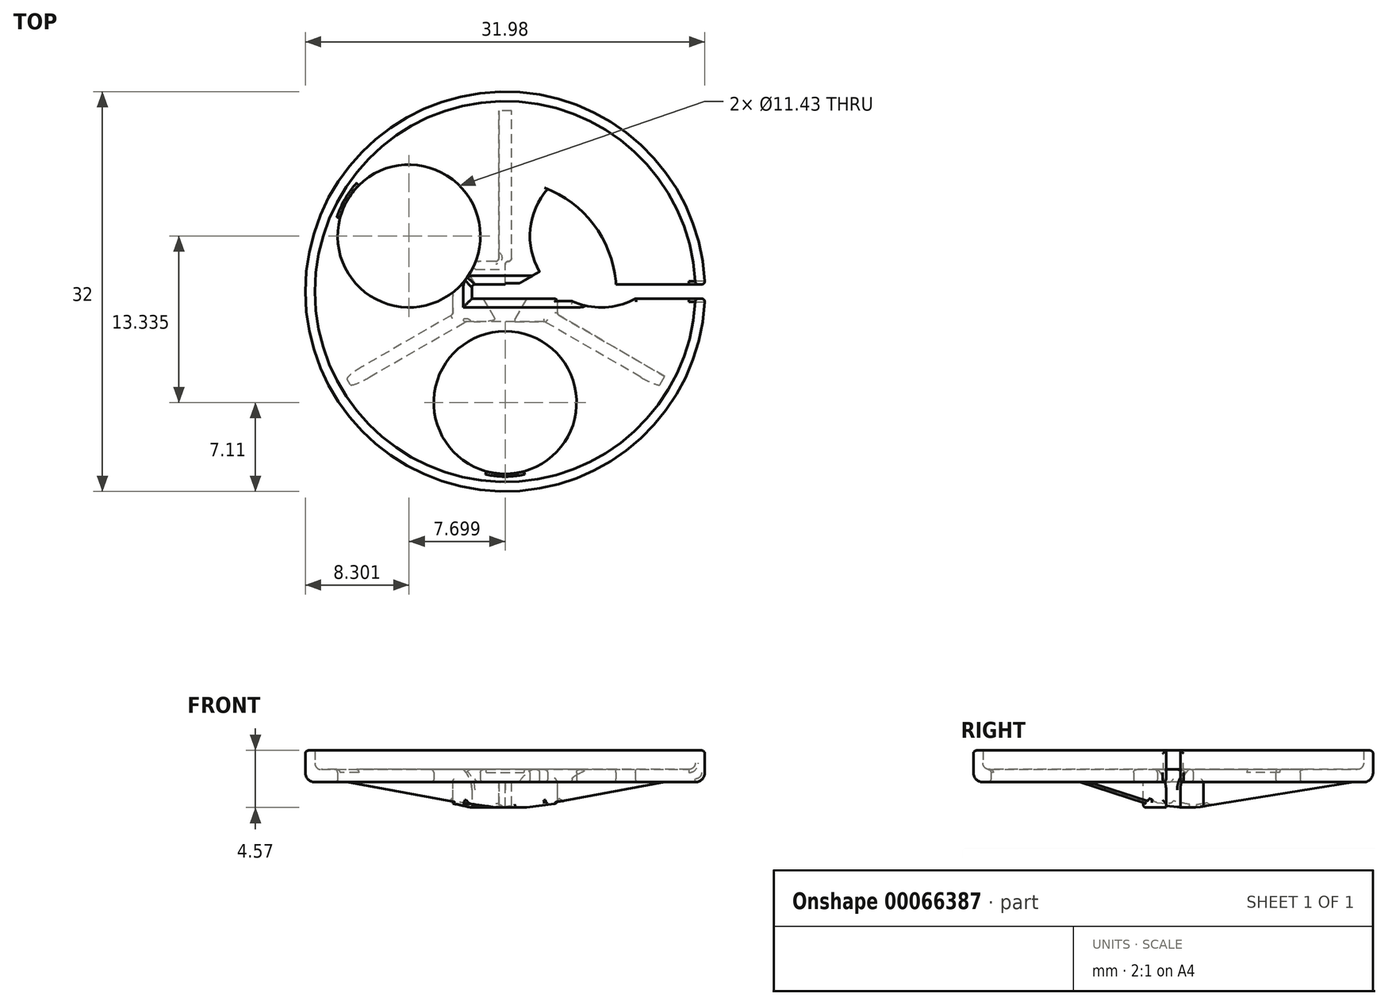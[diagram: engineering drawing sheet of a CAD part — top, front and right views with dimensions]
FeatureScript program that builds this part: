
annotation { "Feature Type Name" : "Feature", "Feature Type Description" : "" }
export const myFeature = defineFeature(function(context is Context, id is Id, definition is map)
    precondition{}
    {
        {
            var Q0;
            Q0=qCreatedBy(makeId("Top.planeOp"),FACE);
            var sketch = newSketch(context, id + "F0", { "sketchPlane" : qUnion([Q0])});
            skCircle(sketch, "E0", {"center": v(0, 0) * mm, "radius": 15.24 * mm});
            skCircle(sketch, "E1", {"center": v(0, 0) * mm, "radius": 16 * mm});
            skLineSegment(sketch, "E2.rect.bottom", {"start": v(20.24, 0.57) * mm, "end": v(-2.67, 0.57) * mm});
            skLineSegment(sketch, "E2.rect.top", {"start": v(20.24, -0.57) * mm, "end": v(-2.67, -0.57) * mm});
            skLineSegment(sketch, "E2.rect.left", {"start": v(20.24, 0.57) * mm, "end": v(20.24, -0.57) * mm});
            skLineSegment(sketch, "E2.rect.right", {"start": v(-2.67, 0.57) * mm, "end": v(-2.67, -0.57) * mm});
            skPoint(sketch, "E2.rect.middle", {"position": v(8.79, 0) * mm});
            skLineSegment(sketch, "E3.rect.bottom", {"start": v(1.65, 13.2) * mm, "end": v(-1.65, 13.2) * mm});
            skLineSegment(sketch, "E3.rect.top", {"start": v(1.65, 11.68) * mm, "end": v(-1.65, 11.68) * mm});
            skLineSegment(sketch, "E3.rect.left", {"start": v(1.65, 13.2) * mm, "end": v(1.65, 11.68) * mm});
            skLineSegment(sketch, "E3.rect.right", {"start": v(-1.65, 13.2) * mm, "end": v(-1.65, 11.68) * mm});
            skPoint(sketch, "E3.rect.middle", {"position": v(0, 12.45) * mm});
            skLineSegment(sketch, "E4", {"start": v(0, 0) * mm, "end": v(-13.86, -8) * mm});
            skLineSegment(sketch, "E5", {"start": v(0, 0) * mm, "end": v(13.86, -8) * mm});
            skLineSegment(sketch, "E6", {"start": v(-12.26, -5.17) * mm, "end": v(-10.61, -8.03) * mm});
            skLineSegment(sketch, "E7", {"start": v(-10.61, -8.03) * mm, "end": v(-9.3, -7.27) * mm});
            skLineSegment(sketch, "E8", {"start": v(-9.3, -7.27) * mm, "end": v(-10.94, -4.41) * mm});
            skLineSegment(sketch, "E9", {"start": v(-10.94, -4.41) * mm, "end": v(-12.26, -5.17) * mm});
            skLineSegment(sketch, "E10", {"start": v(12.26, -5.17) * mm, "end": v(10.61, -8.03) * mm});
            skLineSegment(sketch, "E11", {"start": v(10.61, -8.03) * mm, "end": v(9.3, -7.27) * mm});
            skLineSegment(sketch, "E12", {"start": v(9.3, -7.27) * mm, "end": v(10.94, -4.41) * mm});
            skLineSegment(sketch, "E13", {"start": v(10.94, -4.41) * mm, "end": v(12.26, -5.17) * mm});
            skCircle(sketch, "E14", {"center": v(0, 0) * mm, "radius": 8.9 * mm});
            skLineSegment(sketch, "E15", {"start": v(0, 0) * mm, "end": v(-7.7, 4.44) * mm});
            skLineSegment(sketch, "E16", {"start": v(0, 0) * mm, "end": v(7.7, 4.44) * mm});
            skLineSegment(sketch, "E17", {"start": v(0, 0) * mm, "end": v(0, -8.9) * mm});
            skCircle(sketch, "E18", {"center": v(-7.7, 4.44) * mm, "radius": 5.72 * mm});
            skCircle(sketch, "E19", {"center": v(7.7, 4.44) * mm, "radius": 5.72 * mm});
            skCircle(sketch, "E20", {"center": v(0, -8.9) * mm, "radius": 5.72 * mm});
            skSolve(sketch);
        }
        {
            var Q0;
            {var subQ0=sQuery(id+"F0.wireOp",EDGE,"E2.rect.bottom");var subQ1=sQuery(id+"F0.wireOp",EDGE,"E0");var subQ2=makeQuery(id+"F0.imprint","INTERSECT",VERTEX,{"derivedFrom":[subQ1,subQ0]});Q0=makeQuery(id+"F0.imprint","IMPRINT",FACE,{"disambiguationData":[TD([[makeQuery(id+"F0.imprint","IMPRINT",EDGE,{"disambiguationData":[TD([[subQ2,-1.0]])],"derivedFrom":subQ1}),-1.0]])]});}
            var Q1;
            {var subQ5=sQuery(id+"F0.wireOp",EDGE,"E2.rect.right");Q1=makeQuery(id+"F0.imprint","IMPRINT",FACE,{"disambiguationData":[TD([[makeQuery(id+"F0.imprint","IMPRINT",EDGE,{"derivedFrom":subQ5}),-1.0]])]});}
            var Q2;
            {var subQ1=sQuery(id+"F0.wireOp",EDGE,"E7");Q2=makeQuery(id+"F0.imprint","IMPRINT",FACE,{"disambiguationData":[TD([[makeQuery(id+"F0.imprint","IMPRINT",EDGE,{"derivedFrom":subQ1}),-1.0]])]});}
            var Q3;
            {var subQ5=sQuery(id+"F0.wireOp",EDGE,"E7");Q3=makeQuery(id+"F0.imprint","IMPRINT",FACE,{"disambiguationData":[TD([[makeQuery(id+"F0.imprint","IMPRINT",EDGE,{"derivedFrom":subQ5}),1.0]])]});}
            var Q4;
            {var subQ5=sQuery(id+"F0.wireOp",EDGE,"E9");Q4=makeQuery(id+"F0.imprint","IMPRINT",FACE,{"disambiguationData":[TD([[makeQuery(id+"F0.imprint","IMPRINT",EDGE,{"derivedFrom":subQ5}),1.0]])]});}
            var Q5;
            Q5=makeQuery(id+"F0.imprint","IMPRINT",FACE,{"disambiguationData":[TD([[makeQuery(id+"F0.imprint","IMPRINT",EDGE,{"derivedFrom":sQuery(id+"F0.wireOp",EDGE,"E3.rect.bottom")}),1.0]])]});
            var Q6;
            {var subQ5=sQuery(id+"F0.wireOp",EDGE,"E13");Q6=makeQuery(id+"F0.imprint","IMPRINT",FACE,{"disambiguationData":[TD([[makeQuery(id+"F0.imprint","IMPRINT",EDGE,{"derivedFrom":subQ5}),-1.0]])]});}
            var Q7;
            {var subQ5=sQuery(id+"F0.wireOp",EDGE,"E11");Q7=makeQuery(id+"F0.imprint","IMPRINT",FACE,{"disambiguationData":[TD([[makeQuery(id+"F0.imprint","IMPRINT",EDGE,{"derivedFrom":subQ5}),-1.0]])]});}
            var Q8;
            {var subQ10=sQuery(id+"F0.wireOp",EDGE,"E13");Q8=makeQuery(id+"F0.imprint","IMPRINT",FACE,{"disambiguationData":[TD([[makeQuery(id+"F0.imprint","IMPRINT",EDGE,{"derivedFrom":subQ10}),1.0]])]});}
            var Q9;
            {var subQ0=sQuery(id+"F0.wireOp",EDGE,"E4");var subQ1=sQuery(id+"F0.wireOp",EDGE,"E0");var subQ2=makeQuery(id+"F0.imprint","INTERSECT",VERTEX,{"derivedFrom":[subQ1,subQ0]});Q9=makeQuery(id+"F0.imprint","IMPRINT",FACE,{"disambiguationData":[TD([[makeQuery(id+"F0.imprint","IMPRINT",EDGE,{"disambiguationData":[TD([[subQ2,-1.0]])],"derivedFrom":subQ1}),-1.0]])]});}
            var Q10;
            {var subQ0=sQuery(id+"F0.wireOp",EDGE,"E5");var subQ1=sQuery(id+"F0.wireOp",EDGE,"E0");var subQ2=makeQuery(id+"F0.imprint","INTERSECT",VERTEX,{"derivedFrom":[subQ1,subQ0]});Q10=makeQuery(id+"F0.imprint","IMPRINT",FACE,{"disambiguationData":[TD([[makeQuery(id+"F0.imprint","IMPRINT",EDGE,{"disambiguationData":[TD([[subQ2,-1.0]])],"derivedFrom":subQ1}),-1.0]])]});}
            var Q11;
            Q11=makeQuery(id+"F0.imprint","IMPRINT",FACE,{"disambiguationData":[TD([[makeQuery(id+"F0.imprint","IMPRINT",EDGE,{"derivedFrom":sQuery(id+"F0.wireOp",EDGE,"E3.rect.bottom")}),-1.0]])]});
            var Q12;
            {var subQ1=sQuery(id+"F0.wireOp",EDGE,"E2.rect.bottom");var subQ5=sQuery(id+"F0.wireOp",EDGE,"E16");var subQ6=makeQuery(id+"F0.imprint","INTERSECT",VERTEX,{"derivedFrom":[subQ1,subQ5]});Q12=makeQuery(id+"F0.imprint","IMPRINT",FACE,{"disambiguationData":[TD([[makeQuery(id+"F0.imprint","IMPRINT",EDGE,{"disambiguationData":[TD([[subQ6,-1.0]])],"derivedFrom":subQ1}),-1.0]])]});}
            var Q13;
            {var subQ1=sQuery(id+"F0.wireOp",EDGE,"E2.rect.top");var subQ5=sQuery(id+"F0.wireOp",EDGE,"E5");var subQ6=makeQuery(id+"F0.imprint","INTERSECT",VERTEX,{"derivedFrom":[subQ1,subQ5]});Q13=makeQuery(id+"F0.imprint","IMPRINT",FACE,{"disambiguationData":[TD([[makeQuery(id+"F0.imprint","IMPRINT",EDGE,{"disambiguationData":[TD([[subQ6,-1.0]])],"derivedFrom":subQ1}),1.0]])]});}
            var Q14;
            {var subQ0=sQuery(id+"F0.wireOp",EDGE,"E17");var subQ1=sQuery(id+"F0.wireOp",EDGE,"E2.rect.top");var subQ2=makeQuery(id+"F0.imprint","INTERSECT",VERTEX,{"derivedFrom":[subQ1,subQ0]});Q14=makeQuery(id+"F0.imprint","IMPRINT",FACE,{"disambiguationData":[TD([[makeQuery(id+"F0.imprint","IMPRINT",EDGE,{"disambiguationData":[TD([[subQ2,-1.0]])],"derivedFrom":subQ1}),1.0]])]});}
            var Q15;
            {var subQ0=sQuery(id+"F0.wireOp",EDGE,"E19");var subQ1=sQuery(id+"F0.wireOp",EDGE,"E2.rect.top");var subQ2=makeQuery(id+"F0.imprint","INTERSECT",VERTEX,{"disambiguationData":[OD(1.0)],"derivedFrom":[subQ1,subQ0]});Q15=makeQuery(id+"F0.imprint","IMPRINT",FACE,{"disambiguationData":[TD([[makeQuery(id+"F0.imprint","IMPRINT",EDGE,{"disambiguationData":[TD([[subQ2,-1.0]])],"derivedFrom":subQ1}),1.0]])]});}
            var Q16;
            {var subQ0=sQuery(id+"F0.wireOp",EDGE,"E19");var subQ1=sQuery(id+"F0.wireOp",EDGE,"E2.rect.bottom");var subQ2=makeQuery(id+"F0.imprint","INTERSECT",VERTEX,{"disambiguationData":[OD(1.0)],"derivedFrom":[subQ1,subQ0]});Q16=makeQuery(id+"F0.imprint","IMPRINT",FACE,{"disambiguationData":[TD([[makeQuery(id+"F0.imprint","IMPRINT",EDGE,{"disambiguationData":[TD([[subQ2,-1.0]])],"derivedFrom":subQ1}),-1.0]])]});}
            extrude(context, id + "F1", {"entities" : qUnion([Q0, Q1, Q2, Q3, Q4, Q5, Q6, Q7, Q8, Q9, Q10, Q11, Q12, Q13, Q14, Q15, Q16]), "depth" : 1.02 * mm});
        }
        {
            var Q0;
            {var subQ0=sQuery(id+"F0.wireOp",EDGE,"E2.rect.bottom");var subQ1=sQuery(id+"F0.wireOp",EDGE,"E0");var subQ2=makeQuery(id+"F0.imprint","INTERSECT",VERTEX,{"derivedFrom":[subQ1,subQ0]});Q0=makeQuery(id+"F0.imprint","IMPRINT",FACE,{"disambiguationData":[TD([[makeQuery(id+"F0.imprint","IMPRINT",EDGE,{"disambiguationData":[TD([[subQ2,-1.0]])],"derivedFrom":subQ1}),-1.0]])]});}
            var Q1;
            {var subQ0=sQuery(id+"F0.wireOp",EDGE,"E4");var subQ1=sQuery(id+"F0.wireOp",EDGE,"E0");var subQ2=makeQuery(id+"F0.imprint","INTERSECT",VERTEX,{"derivedFrom":[subQ1,subQ0]});Q1=makeQuery(id+"F0.imprint","IMPRINT",FACE,{"disambiguationData":[TD([[makeQuery(id+"F0.imprint","IMPRINT",EDGE,{"disambiguationData":[TD([[subQ2,-1.0]])],"derivedFrom":subQ1}),-1.0]])]});}
            var Q2;
            {var subQ0=sQuery(id+"F0.wireOp",EDGE,"E5");var subQ1=sQuery(id+"F0.wireOp",EDGE,"E0");var subQ2=makeQuery(id+"F0.imprint","INTERSECT",VERTEX,{"derivedFrom":[subQ1,subQ0]});Q2=makeQuery(id+"F0.imprint","IMPRINT",FACE,{"disambiguationData":[TD([[makeQuery(id+"F0.imprint","IMPRINT",EDGE,{"disambiguationData":[TD([[subQ2,-1.0]])],"derivedFrom":subQ1}),-1.0]])]});}
            extrude(context, id + "F2", {"entities" : qUnion([Q0, Q1, Q2]), "operationType" : NewBodyOperationType.ADD, "depth" : 2.54 * mm});
        }
        {
            var Q0;
            Q0=makeQuery(id+"F1.opExtrude","CAP_FACE",FACE,{"disambiguationData":[OSD([sQuery(id+"F0.wireOp",EDGE,"E1"),sQuery(id+"F0.wireOp",EDGE,"E2.rect.bottom"),sQuery(id+"F0.wireOp",EDGE,"E2.rect.top"),sQuery(id+"F0.wireOp",EDGE,"E2.rect.right"),sQuery(id+"F0.wireOp",EDGE,"E18"),sQuery(id+"F0.wireOp",EDGE,"E19"),sQuery(id+"F0.wireOp",EDGE,"E20")])],"isStart":true});
            var sketch = newSketch(context, id + "F3", { "sketchPlane" : qUnion([Q0])});
            skLineSegment(sketch, "E21.rect.bottom", {"start": v(4.2, 2.41) * mm, "end": v(-4.2, 2.41) * mm});
            skLineSegment(sketch, "E21.rect.top", {"start": v(4.2, -2.41) * mm, "end": v(-4.2, -2.41) * mm});
            skLineSegment(sketch, "E21.rect.left", {"start": v(4.2, 2.41) * mm, "end": v(4.2, -2.41) * mm});
            skLineSegment(sketch, "E21.rect.right", {"start": v(-4.2, 2.41) * mm, "end": v(-4.2, -2.41) * mm});
            skPoint(sketch, "E21.rect.middle", {"position": v(0, 0) * mm});
            skLineSegment(sketch, "E22", {"start": v(0, 0) * mm, "end": v(-13.86, 8) * mm});
            skLineSegment(sketch, "E23", {"start": v(0, 0) * mm, "end": v(13.86, 8) * mm});
            skLineSegment(sketch, "E24", {"start": v(0, 0) * mm, "end": v(0, -16) * mm});
            skLineSegment(sketch, "E25.bottom", {"start": v(-0.5, -2.41) * mm, "end": v(0.5, -2.41) * mm});
            skLineSegment(sketch, "E25.top", {"start": v(-0.5, -14.48) * mm, "end": v(0.5, -14.48) * mm});
            skLineSegment(sketch, "E25.left", {"start": v(-0.5, -2.41) * mm, "end": v(-0.5, -14.48) * mm});
            skLineSegment(sketch, "E25.right", {"start": v(0.5, -2.41) * mm, "end": v(0.5, -14.48) * mm});
            skLineSegment(sketch, "E26", {"start": v(-4.2, 1.83) * mm, "end": v(-12.8, 6.8) * mm});
            skLineSegment(sketch, "E27", {"start": v(-12.8, 6.8) * mm, "end": v(-12.28, 7.68) * mm});
            skLineSegment(sketch, "E28", {"start": v(-12.28, 7.68) * mm, "end": v(-3.16, 2.41) * mm});
            skLineSegment(sketch, "E29", {"start": v(4.2, 1.83) * mm, "end": v(12.8, 6.8) * mm});
            skLineSegment(sketch, "E30", {"start": v(12.8, 6.8) * mm, "end": v(12.28, 7.68) * mm});
            skLineSegment(sketch, "E31", {"start": v(12.28, 7.68) * mm, "end": v(3.16, 2.41) * mm});
            skSolve(sketch);
        }
        {
            var Q0;
            {var subQ1=sQuery(id+"F3.wireOp",EDGE,"E21.rect.bottom");Q0=makeQuery(id+"F3.imprint","IMPRINT",FACE,{"disambiguationData":[TD([[makeQuery(id+"F3.imprint","IMPRINT",EDGE,{"derivedFrom":subQ1}),1.0]])]});}
            var Q1;
            {var subQ0=sQuery(id+"F3.wireOp",EDGE,"E28");Q1=makeQuery(id+"F3.imprint","IMPRINT",FACE,{"disambiguationData":[TD([[makeQuery(id+"F3.imprint","IMPRINT",EDGE,{"derivedFrom":subQ0}),-1.0]])]});}
            var Q2;
            {var subQ0=sQuery(id+"F3.wireOp",EDGE,"E26");Q2=makeQuery(id+"F3.imprint","IMPRINT",FACE,{"disambiguationData":[TD([[makeQuery(id+"F3.imprint","IMPRINT",EDGE,{"derivedFrom":subQ0}),-1.0]])]});}
            var Q3;
            {var subQ0=sQuery(id+"F0.wireOp",EDGE,"E2.rect.right");var subQ1=makeQuery(id+"F1.opExtrude","CAP_EDGE",EDGE,{"disambiguationData":[OSD([subQ0])],"isStart":true});Q3=makeQuery(id+"F3.imprint","IMPRINT",FACE,{"disambiguationData":[TD([[makeQuery(id+"F3.imprint","IMPRINT",EDGE,{"derivedFrom":subQ1}),1.0]])]});}
            var Q4;
            {var subQ11=sQuery(id+"F3.wireOp",EDGE,"E24");var subQ13=sQuery(id+"F3.wireOp",EDGE,"E25.bottom");var subQ16=makeQuery(id+"F3.imprint","INTERSECT",VERTEX,{"derivedFrom":[subQ11,subQ13]});Q4=makeQuery(id+"F3.imprint","IMPRINT",FACE,{"disambiguationData":[TD([[makeQuery(id+"F3.imprint","IMPRINT",EDGE,{"disambiguationData":[TD([[subQ16,-1.0]])],"derivedFrom":subQ13}),1.0]])]});}
            var Q5;
            {var subQ1=sQuery(id+"F3.wireOp",EDGE,"E21.rect.bottom");var subQ9=sQuery(id+"F3.wireOp",EDGE,"E21.rect.left");var subQ10=makeQuery(id+"F3.imprint","INTERSECT",VERTEX,{"derivedFrom":[subQ1,subQ9]});Q5=makeQuery(id+"F3.imprint","IMPRINT",FACE,{"disambiguationData":[TD([[makeQuery(id+"F3.imprint","IMPRINT",EDGE,{"disambiguationData":[TD([[subQ10,-1.0]])],"derivedFrom":subQ1}),1.0]])]});}
            var Q6;
            {var subQ0=sQuery(id+"F3.wireOp",EDGE,"E29");Q6=makeQuery(id+"F3.imprint","IMPRINT",FACE,{"disambiguationData":[TD([[makeQuery(id+"F3.imprint","IMPRINT",EDGE,{"derivedFrom":subQ0}),1.0]])]});}
            var Q7;
            {var subQ0=sQuery(id+"F3.wireOp",EDGE,"E31");Q7=makeQuery(id+"F3.imprint","IMPRINT",FACE,{"disambiguationData":[TD([[makeQuery(id+"F3.imprint","IMPRINT",EDGE,{"derivedFrom":subQ0}),1.0]])]});}
            var Q8;
            {var subQ5=sQuery(id+"F3.wireOp",EDGE,"E25.right");Q8=makeQuery(id+"F3.imprint","IMPRINT",FACE,{"disambiguationData":[TD([[makeQuery(id+"F3.imprint","IMPRINT",EDGE,{"derivedFrom":subQ5}),-1.0]])]});}
            var Q9;
            {var subQ5=sQuery(id+"F3.wireOp",EDGE,"E25.left");Q9=makeQuery(id+"F3.imprint","IMPRINT",FACE,{"disambiguationData":[TD([[makeQuery(id+"F3.imprint","IMPRINT",EDGE,{"derivedFrom":subQ5}),1.0]])]});}
            extrude(context, id + "F4", {"entities" : qUnion([Q0, Q1, Q2, Q3, Q4, Q5, Q6, Q7, Q8, Q9]), "operationType" : NewBodyOperationType.ADD, "depth" : 2.03 * mm});
        }
        {
            var Q0;
            {var subQ0=sQuery(id+"F0.wireOp",EDGE,"E2.rect.bottom");var subQ2=makeQuery(id+"F0.imprint","INTERSECT",VERTEX,{"derivedFrom":[subQ0,sQuery(id+"F0.wireOp",EDGE,"E16")]});Q0=makeQuery(id+"F1.opExtrude","CAP_EDGE",EDGE,{"disambiguationData":[OSD([subQ0]),TDD([makeQuery(id+"F0.imprint","IMPRINT",EDGE,{"disambiguationData":[TD([[makeQuery(id+"F0.imprint","INTERSECT",VERTEX,{"disambiguationData":[OD(1.0)],"derivedFrom":[subQ0,sQuery(id+"F0.wireOp",EDGE,"E19")]}),-1.0]])],"derivedFrom":subQ0}),makeQuery(id+"F0.imprint","IMPRINT",EDGE,{"disambiguationData":[TD([[subQ2,-1.0]])],"derivedFrom":subQ0}),makeQuery(id+"F0.imprint","IMPRINT",EDGE,{"disambiguationData":[TD([[makeQuery(id+"F0.imprint","INTERSECT",VERTEX,{"derivedFrom":[subQ0,sQuery(id+"F0.wireOp",EDGE,"E2.rect.right")]}),1.0]])],"derivedFrom":subQ0})])],"isStart":false});}
            var Q1;
            {var subQ0=sQuery(id+"F0.wireOp",EDGE,"E2.rect.top");var subQ2=makeQuery(id+"F0.imprint","INTERSECT",VERTEX,{"derivedFrom":[subQ0,sQuery(id+"F0.wireOp",EDGE,"E17")]});var subQ3=makeQuery(id+"F0.imprint","INTERSECT",VERTEX,{"derivedFrom":[subQ0,sQuery(id+"F0.wireOp",EDGE,"E5")]});Q1=makeQuery(id+"F1.opExtrude","CAP_EDGE",EDGE,{"disambiguationData":[OSD([subQ0]),TDD([makeQuery(id+"F0.imprint","IMPRINT",EDGE,{"disambiguationData":[TD([[makeQuery(id+"F0.imprint","INTERSECT",VERTEX,{"disambiguationData":[OD(1.0)],"derivedFrom":[subQ0,sQuery(id+"F0.wireOp",EDGE,"E19")]}),-1.0]])],"derivedFrom":subQ0}),makeQuery(id+"F0.imprint","IMPRINT",EDGE,{"disambiguationData":[TD([[subQ3,-1.0]])],"derivedFrom":subQ0}),makeQuery(id+"F0.imprint","IMPRINT",EDGE,{"disambiguationData":[TD([[subQ2,-1.0]])],"derivedFrom":subQ0}),makeQuery(id+"F0.imprint","IMPRINT",EDGE,{"disambiguationData":[TD([[makeQuery(id+"F0.imprint","INTERSECT",VERTEX,{"derivedFrom":[subQ0,sQuery(id+"F0.wireOp",EDGE,"E2.rect.right")]}),1.0]])],"derivedFrom":subQ0})])],"isStart":false});}
            var Q2;
            Q2=makeQuery(id+"F1.opExtrude","CAP_EDGE",EDGE,{"disambiguationData":[OSD([sQuery(id+"F0.wireOp",EDGE,"E2.rect.right")])],"isStart":false});
            chamfer(context, id + "F5", {"entities" : qUnion([Q0, Q1, Q2]), "width" : 0.69 * mm, "tangentPropagation" : true});
        }
        {
            var Q0;
            {var subQ0=sQuery(id+"F0.wireOp",EDGE,"E2.rect.bottom");var subQ2=makeQuery(id+"F0.imprint","IMPRINT",EDGE,{"disambiguationData":[TD([[makeQuery(id+"F0.imprint","INTERSECT",VERTEX,{"derivedFrom":[subQ0,sQuery(id+"F0.wireOp",EDGE,"E2.rect.right")]}),1.0]])],"derivedFrom":subQ0});var subQ3=makeQuery(id+"F0.imprint","INTERSECT",VERTEX,{"derivedFrom":[subQ0,sQuery(id+"F0.wireOp",EDGE,"E16")]});var subQ4=makeQuery(id+"F0.imprint","IMPRINT",EDGE,{"disambiguationData":[TD([[subQ3,-1.0]])],"derivedFrom":subQ0});var subQ5=makeQuery(id+"F0.imprint","IMPRINT",EDGE,{"disambiguationData":[TD([[makeQuery(id+"F0.imprint","INTERSECT",VERTEX,{"disambiguationData":[OD(1.0)],"derivedFrom":[subQ0,sQuery(id+"F0.wireOp",EDGE,"E19")]}),-1.0]])],"derivedFrom":subQ0});Q0=makeQuery(id+"F5.opChamfer","BLEND_EDGE",EDGE,{"blendedFrom":[makeQuery(id+"F1.opExtrude","CAP_EDGE",EDGE,{"disambiguationData":[OSD([subQ0]),TDD([subQ5,subQ4,subQ2])],"isStart":false}),makeQuery(id+"F4.boolean.opBoolean","MERGE",FACE,{"derivedFrom":[makeQuery(id+"F1.opExtrude","SWEPT_FACE",FACE,{"disambiguationData":[OSD([subQ0]),TDD([subQ5,subQ4,subQ2])]}),makeQuery(id+"F4.opExtrude","SWEPT_FACE",FACE,{"disambiguationData":[OSD([subQ0])]})]})],"blendedInto":[makeQuery(id+"F4.boolean.opBoolean","MERGE",FACE,{"derivedFrom":[makeQuery(id+"F1.opExtrude","SWEPT_FACE",FACE,{"disambiguationData":[OSD([subQ0]),TDD([subQ5,subQ4,subQ2])]}),makeQuery(id+"F4.opExtrude","SWEPT_FACE",FACE,{"disambiguationData":[OSD([subQ0])]})]})]});}
            var Q1;
            {var subQ0=sQuery(id+"F0.wireOp",EDGE,"E2.rect.right");Q1=makeQuery(id+"F5.opChamfer","BLEND_EDGE",EDGE,{"blendedFrom":[makeQuery(id+"F1.opExtrude","CAP_EDGE",EDGE,{"disambiguationData":[OSD([subQ0])],"isStart":false}),makeQuery(id+"F4.boolean.opBoolean","MERGE",FACE,{"derivedFrom":[makeQuery(id+"F1.opExtrude","SWEPT_FACE",FACE,{"disambiguationData":[OSD([subQ0])]}),makeQuery(id+"F4.opExtrude","SWEPT_FACE",FACE,{"disambiguationData":[OSD([subQ0])]})]})],"blendedInto":[makeQuery(id+"F4.boolean.opBoolean","MERGE",FACE,{"derivedFrom":[makeQuery(id+"F1.opExtrude","SWEPT_FACE",FACE,{"disambiguationData":[OSD([subQ0])]}),makeQuery(id+"F4.opExtrude","SWEPT_FACE",FACE,{"disambiguationData":[OSD([subQ0])]})]})]});}
            var Q2;
            {var subQ0=sQuery(id+"F0.wireOp",EDGE,"E2.rect.top");var subQ2=makeQuery(id+"F0.imprint","IMPRINT",EDGE,{"disambiguationData":[TD([[makeQuery(id+"F0.imprint","INTERSECT",VERTEX,{"derivedFrom":[subQ0,sQuery(id+"F0.wireOp",EDGE,"E2.rect.right")]}),1.0]])],"derivedFrom":subQ0});var subQ3=makeQuery(id+"F0.imprint","INTERSECT",VERTEX,{"derivedFrom":[subQ0,sQuery(id+"F0.wireOp",EDGE,"E17")]});var subQ4=makeQuery(id+"F0.imprint","IMPRINT",EDGE,{"disambiguationData":[TD([[subQ3,-1.0]])],"derivedFrom":subQ0});var subQ5=makeQuery(id+"F0.imprint","INTERSECT",VERTEX,{"derivedFrom":[subQ0,sQuery(id+"F0.wireOp",EDGE,"E5")]});var subQ6=makeQuery(id+"F0.imprint","IMPRINT",EDGE,{"disambiguationData":[TD([[subQ5,-1.0]])],"derivedFrom":subQ0});var subQ7=makeQuery(id+"F0.imprint","IMPRINT",EDGE,{"disambiguationData":[TD([[makeQuery(id+"F0.imprint","INTERSECT",VERTEX,{"disambiguationData":[OD(1.0)],"derivedFrom":[subQ0,sQuery(id+"F0.wireOp",EDGE,"E19")]}),-1.0]])],"derivedFrom":subQ0});Q2=makeQuery(id+"F5.opChamfer","BLEND_EDGE",EDGE,{"blendedFrom":[makeQuery(id+"F1.opExtrude","CAP_EDGE",EDGE,{"disambiguationData":[OSD([subQ0]),TDD([subQ7,subQ6,subQ4,subQ2])],"isStart":false}),makeQuery(id+"F4.boolean.opBoolean","MERGE",FACE,{"derivedFrom":[makeQuery(id+"F1.opExtrude","SWEPT_FACE",FACE,{"disambiguationData":[OSD([subQ0]),TDD([subQ7,subQ6,subQ4,subQ2])]}),makeQuery(id+"F4.opExtrude","SWEPT_FACE",FACE,{"disambiguationData":[OSD([subQ0])]})]})],"blendedInto":[makeQuery(id+"F4.boolean.opBoolean","MERGE",FACE,{"derivedFrom":[makeQuery(id+"F1.opExtrude","SWEPT_FACE",FACE,{"disambiguationData":[OSD([subQ0]),TDD([subQ7,subQ6,subQ4,subQ2])]}),makeQuery(id+"F4.opExtrude","SWEPT_FACE",FACE,{"disambiguationData":[OSD([subQ0])]})]})]});}
            fillet(context, id + "F6", {"entities" : qUnion([Q0, Q1, Q2]), "radius" : 2.31 * mm, "tangentPropagation" : true, "allowEdgeOverflow" : false});
        }
        {
            var Q0;
            Q0=makeQuery(id+"F2.boolean.opBoolean","INTERSECT",EDGE,{"derivedFrom":[makeQuery(id+"F1.opExtrude","CAP_FACE",FACE,{"disambiguationData":[OSD([sQuery(id+"F0.wireOp",EDGE,"E1"),sQuery(id+"F0.wireOp",EDGE,"E2.rect.bottom"),sQuery(id+"F0.wireOp",EDGE,"E2.rect.top"),sQuery(id+"F0.wireOp",EDGE,"E2.rect.right"),sQuery(id+"F0.wireOp",EDGE,"E18"),sQuery(id+"F0.wireOp",EDGE,"E19"),sQuery(id+"F0.wireOp",EDGE,"E20")])],"isStart":false}),makeQuery(id+"F2.opExtrude","SWEPT_FACE",FACE,{"disambiguationData":[OSD([sQuery(id+"F0.wireOp",EDGE,"E0")])]})]});
            fillet(context, id + "F7", {"entities" : qUnion([Q0]), "radius" : 0.5 * mm, "tangentPropagation" : true, "allowEdgeOverflow" : false});
        }
        {
            var Q0;
            Q0=makeQuery(id+"F1.opExtrude","CAP_EDGE",EDGE,{"disambiguationData":[OSD([sQuery(id+"F0.wireOp",EDGE,"E1")])],"isStart":true});
            fillet(context, id + "F8", {"entities" : qUnion([Q0]), "radius" : 0.76 * mm, "tangentPropagation" : true, "allowEdgeOverflow" : false});
        }
        {
            var Q0;
            Q0=makeQuery(id+"F1.opExtrude","CAP_EDGE",EDGE,{"disambiguationData":[OSD([sQuery(id+"F0.wireOp",EDGE,"E18")])],"isStart":false});
            var Q1;
            {var subQ0=sQuery(id+"F0.wireOp",EDGE,"E19");var subQ1=sQuery(id+"F0.wireOp",EDGE,"E2.rect.bottom");var subQ2=makeQuery(id+"F0.imprint","INTERSECT",VERTEX,{"disambiguationData":[OD(0.0)],"derivedFrom":[sQuery(id+"F0.wireOp",EDGE,"E14"),subQ0]});Q1=makeQuery(id+"F1.opExtrude","CAP_EDGE",EDGE,{"disambiguationData":[OSD([subQ0]),TDD([makeQuery(id+"F0.imprint","IMPRINT",EDGE,{"disambiguationData":[TD([[subQ2,-1.0]])],"derivedFrom":subQ0}),makeQuery(id+"F0.imprint","IMPRINT",EDGE,{"disambiguationData":[TD([[makeQuery(id+"F0.imprint","INTERSECT",VERTEX,{"disambiguationData":[OD(1.0)],"derivedFrom":[subQ1,subQ0]}),1.0]])],"derivedFrom":subQ0}),makeQuery(id+"F0.imprint","IMPRINT",EDGE,{"disambiguationData":[TD([[makeQuery(id+"F0.imprint","INTERSECT",VERTEX,{"disambiguationData":[OD(0.0)],"derivedFrom":[subQ1,subQ0]}),-1.0]])],"derivedFrom":subQ0})])],"isStart":false});}
            var Q2;
            Q2=makeQuery(id+"F1.opExtrude","CAP_EDGE",EDGE,{"disambiguationData":[OSD([sQuery(id+"F0.wireOp",EDGE,"E20")])],"isStart":false});
            var Q3;
            {var subQ0=sQuery(id+"F0.wireOp",EDGE,"E19");var subQ1=sQuery(id+"F0.wireOp",EDGE,"E2.rect.top");Q3=makeQuery(id+"F1.opExtrude","CAP_EDGE",EDGE,{"disambiguationData":[OSD([subQ0]),TDD([makeQuery(id+"F0.imprint","IMPRINT",EDGE,{"disambiguationData":[TD([[makeQuery(id+"F0.imprint","INTERSECT",VERTEX,{"disambiguationData":[OD(1.0)],"derivedFrom":[subQ1,subQ0]}),-1.0]])],"derivedFrom":subQ0}),makeQuery(id+"F0.imprint","IMPRINT",EDGE,{"disambiguationData":[TD([[makeQuery(id+"F0.imprint","INTERSECT",VERTEX,{"disambiguationData":[OD(0.0)],"derivedFrom":[subQ1,subQ0]}),1.0]])],"derivedFrom":subQ0})])],"isStart":false});}
            var Q4;
            Q4=makeQuery(id+"F1.opExtrude","CAP_EDGE",EDGE,{"disambiguationData":[OSD([sQuery(id+"F0.wireOp",EDGE,"E20")])],"isStart":true});
            var Q5;
            {var subQ0=sQuery(id+"F0.wireOp",EDGE,"E19");var subQ1=sQuery(id+"F0.wireOp",EDGE,"E2.rect.bottom");var subQ2=makeQuery(id+"F0.imprint","INTERSECT",VERTEX,{"disambiguationData":[OD(0.0)],"derivedFrom":[sQuery(id+"F0.wireOp",EDGE,"E14"),subQ0]});Q5=makeQuery(id+"F1.opExtrude","CAP_EDGE",EDGE,{"disambiguationData":[OSD([subQ0]),TDD([makeQuery(id+"F0.imprint","IMPRINT",EDGE,{"disambiguationData":[TD([[subQ2,-1.0]])],"derivedFrom":subQ0}),makeQuery(id+"F0.imprint","IMPRINT",EDGE,{"disambiguationData":[TD([[makeQuery(id+"F0.imprint","INTERSECT",VERTEX,{"disambiguationData":[OD(1.0)],"derivedFrom":[subQ1,subQ0]}),1.0]])],"derivedFrom":subQ0}),makeQuery(id+"F0.imprint","IMPRINT",EDGE,{"disambiguationData":[TD([[makeQuery(id+"F0.imprint","INTERSECT",VERTEX,{"disambiguationData":[OD(0.0)],"derivedFrom":[subQ1,subQ0]}),-1.0]])],"derivedFrom":subQ0})])],"isStart":true});}
            var Q6;
            Q6=makeQuery(id+"F1.opExtrude","CAP_EDGE",EDGE,{"disambiguationData":[OSD([sQuery(id+"F0.wireOp",EDGE,"E18")])],"isStart":true});
            var Q7;
            Q7=makeQuery(id+"F2.opExtrude","CAP_EDGE",EDGE,{"disambiguationData":[OSD([sQuery(id+"F0.wireOp",EDGE,"E1")])],"isStart":false});
            var Q8;
            {var subQ0=sQuery(id+"F0.wireOp",EDGE,"E19");var subQ1=sQuery(id+"F0.wireOp",EDGE,"E2.rect.top");Q8=makeQuery(id+"F1.opExtrude","CAP_EDGE",EDGE,{"disambiguationData":[OSD([subQ0]),TDD([makeQuery(id+"F0.imprint","IMPRINT",EDGE,{"disambiguationData":[TD([[makeQuery(id+"F0.imprint","INTERSECT",VERTEX,{"disambiguationData":[OD(1.0)],"derivedFrom":[subQ1,subQ0]}),-1.0]])],"derivedFrom":subQ0}),makeQuery(id+"F0.imprint","IMPRINT",EDGE,{"disambiguationData":[TD([[makeQuery(id+"F0.imprint","INTERSECT",VERTEX,{"disambiguationData":[OD(0.0)],"derivedFrom":[subQ1,subQ0]}),1.0]])],"derivedFrom":subQ0})])],"isStart":true});}
            var Q9;
            {var subQ0=sQuery(id+"F0.wireOp",EDGE,"E19");var subQ1=sQuery(id+"F0.wireOp",EDGE,"E2.rect.right");var subQ2=sQuery(id+"F0.wireOp",EDGE,"E2.rect.top");var subQ4=makeQuery(id+"F0.imprint","IMPRINT",EDGE,{"disambiguationData":[TD([[makeQuery(id+"F0.imprint","INTERSECT",VERTEX,{"derivedFrom":[subQ2,subQ1]}),1.0]])],"derivedFrom":subQ2});var subQ5=makeQuery(id+"F0.imprint","INTERSECT",VERTEX,{"derivedFrom":[subQ2,sQuery(id+"F0.wireOp",EDGE,"E17")]});var subQ6=makeQuery(id+"F0.imprint","IMPRINT",EDGE,{"disambiguationData":[TD([[subQ5,-1.0]])],"derivedFrom":subQ2});var subQ7=makeQuery(id+"F0.imprint","INTERSECT",VERTEX,{"derivedFrom":[subQ2,sQuery(id+"F0.wireOp",EDGE,"E5")]});var subQ8=makeQuery(id+"F0.imprint","IMPRINT",EDGE,{"disambiguationData":[TD([[subQ7,-1.0]])],"derivedFrom":subQ2});var subQ9=makeQuery(id+"F0.imprint","IMPRINT",EDGE,{"disambiguationData":[TD([[makeQuery(id+"F0.imprint","INTERSECT",VERTEX,{"disambiguationData":[OD(1.0)],"derivedFrom":[subQ2,subQ0]}),-1.0]])],"derivedFrom":subQ2});Q9=makeQuery(id+"F6.opFillet","BLEND_EDGE",EDGE,{"blendedFrom":[makeQuery(id+"F5.opChamfer","BLEND_EDGE",EDGE,{"blendedFrom":[makeQuery(id+"F1.opExtrude","CAP_EDGE",EDGE,{"disambiguationData":[OSD([subQ2]),TDD([subQ9,subQ8,subQ6,subQ4])],"isStart":false}),makeQuery(id+"F4.boolean.opBoolean","MERGE",FACE,{"derivedFrom":[makeQuery(id+"F1.opExtrude","SWEPT_FACE",FACE,{"disambiguationData":[OSD([subQ2]),TDD([subQ9,subQ8,subQ6,subQ4])]}),makeQuery(id+"F4.opExtrude","SWEPT_FACE",FACE,{"disambiguationData":[OSD([subQ2])]})]})],"blendedInto":[makeQuery(id+"F4.boolean.opBoolean","MERGE",FACE,{"derivedFrom":[makeQuery(id+"F1.opExtrude","SWEPT_FACE",FACE,{"disambiguationData":[OSD([subQ2]),TDD([subQ9,subQ8,subQ6,subQ4])]}),makeQuery(id+"F4.opExtrude","SWEPT_FACE",FACE,{"disambiguationData":[OSD([subQ2])]})]})]}),makeQuery(id+"F1.opExtrude","CAP_FACE",FACE,{"disambiguationData":[OSD([sQuery(id+"F0.wireOp",EDGE,"E1"),sQuery(id+"F0.wireOp",EDGE,"E2.rect.bottom"),subQ2,subQ1,sQuery(id+"F0.wireOp",EDGE,"E18"),subQ0,sQuery(id+"F0.wireOp",EDGE,"E20")])],"isStart":true})],"blendedInto":[makeQuery(id+"F1.opExtrude","CAP_FACE",FACE,{"disambiguationData":[OSD([sQuery(id+"F0.wireOp",EDGE,"E1"),sQuery(id+"F0.wireOp",EDGE,"E2.rect.bottom"),subQ2,subQ1,sQuery(id+"F0.wireOp",EDGE,"E18"),subQ0,sQuery(id+"F0.wireOp",EDGE,"E20")])],"isStart":true})]});}
            var Q10;
            {var subQ0=sQuery(id+"F0.wireOp",EDGE,"E2.rect.top");var subQ1=makeQuery(id+"F0.imprint","INTERSECT",VERTEX,{"derivedFrom":[sQuery(id+"F0.wireOp",EDGE,"E0"),subQ0]});Q10=makeQuery(id+"F1.opExtrude","CAP_EDGE",EDGE,{"disambiguationData":[OSD([subQ0]),TDD([makeQuery(id+"F0.imprint","IMPRINT",EDGE,{"disambiguationData":[TD([[makeQuery(id+"F0.imprint","INTERSECT",VERTEX,{"derivedFrom":[sQuery(id+"F0.wireOp",EDGE,"E1"),subQ0]}),-1.0]])],"derivedFrom":subQ0}),makeQuery(id+"F0.imprint","IMPRINT",EDGE,{"disambiguationData":[TD([[subQ1,-1.0]])],"derivedFrom":subQ0})])],"isStart":true});}
            var Q11;
            {var subQ0=sQuery(id+"F0.wireOp",EDGE,"E2.rect.bottom");var subQ1=makeQuery(id+"F0.imprint","INTERSECT",VERTEX,{"derivedFrom":[sQuery(id+"F0.wireOp",EDGE,"E0"),subQ0]});Q11=makeQuery(id+"F1.opExtrude","CAP_EDGE",EDGE,{"disambiguationData":[OSD([subQ0]),TDD([makeQuery(id+"F0.imprint","IMPRINT",EDGE,{"disambiguationData":[TD([[makeQuery(id+"F0.imprint","INTERSECT",VERTEX,{"derivedFrom":[sQuery(id+"F0.wireOp",EDGE,"E1"),subQ0]}),-1.0]])],"derivedFrom":subQ0}),makeQuery(id+"F0.imprint","IMPRINT",EDGE,{"disambiguationData":[TD([[subQ1,-1.0]])],"derivedFrom":subQ0})])],"isStart":true});}
            var Q12;
            {var subQ0=sQuery(id+"F0.wireOp",EDGE,"E2.rect.top");var subQ1=makeQuery(id+"F0.imprint","INTERSECT",VERTEX,{"derivedFrom":[sQuery(id+"F0.wireOp",EDGE,"E0"),subQ0]});Q12=makeQuery(id+"F1.opExtrude","CAP_EDGE",EDGE,{"disambiguationData":[OSD([subQ0]),TDD([makeQuery(id+"F0.imprint","IMPRINT",EDGE,{"disambiguationData":[TD([[makeQuery(id+"F0.imprint","INTERSECT",VERTEX,{"derivedFrom":[sQuery(id+"F0.wireOp",EDGE,"E1"),subQ0]}),-1.0]])],"derivedFrom":subQ0}),makeQuery(id+"F0.imprint","IMPRINT",EDGE,{"disambiguationData":[TD([[subQ1,-1.0]])],"derivedFrom":subQ0})])],"isStart":false});}
            var Q13;
            {var subQ0=sQuery(id+"F0.wireOp",EDGE,"E2.rect.bottom");var subQ1=makeQuery(id+"F0.imprint","INTERSECT",VERTEX,{"derivedFrom":[sQuery(id+"F0.wireOp",EDGE,"E0"),subQ0]});Q13=makeQuery(id+"F1.opExtrude","CAP_EDGE",EDGE,{"disambiguationData":[OSD([subQ0]),TDD([makeQuery(id+"F0.imprint","IMPRINT",EDGE,{"disambiguationData":[TD([[makeQuery(id+"F0.imprint","INTERSECT",VERTEX,{"derivedFrom":[sQuery(id+"F0.wireOp",EDGE,"E1"),subQ0]}),-1.0]])],"derivedFrom":subQ0}),makeQuery(id+"F0.imprint","IMPRINT",EDGE,{"disambiguationData":[TD([[subQ1,-1.0]])],"derivedFrom":subQ0})])],"isStart":false});}
            fillet(context, id + "F9", {"entities" : qUnion([Q0, Q1, Q2, Q3, Q4, Q5, Q6, Q7, Q8, Q9, Q10, Q11, Q12, Q13]), "radius" : 0.25 * mm, "tangentPropagation" : true, "allowEdgeOverflow" : false});
        }
        {
            var Q0;
            Q0=makeQuery(id+"F4.opExtrude","CAP_EDGE",EDGE,{"disambiguationData":[OSD([sQuery(id+"F3.wireOp",EDGE,"E25.top")])],"isStart":false});
            var Q1;
            Q1=makeQuery(id+"F4.opExtrude","CAP_EDGE",EDGE,{"disambiguationData":[OSD([sQuery(id+"F3.wireOp",EDGE,"E27")])],"isStart":false});
            var Q2;
            Q2=makeQuery(id+"F4.opExtrude","CAP_EDGE",EDGE,{"disambiguationData":[OSD([sQuery(id+"F3.wireOp",EDGE,"E30")])],"isStart":false});
            chamfer(context, id + "F10", {"entities" : qUnion([Q0, Q1, Q2]), "chamferType" : ChamferType.OFFSET_ANGLE, "width" : 12.7 * mm, "oppositeDirection" : false, "angle" : 9.1 * degree, "tangentPropagation" : true});
        }
        {
            var Q0;
            Q0=makeQuery(id+"F10.opChamfer","BLEND_EDGE",EDGE,{"blendedFrom":[makeQuery(id+"F4.opExtrude","CAP_EDGE",EDGE,{"disambiguationData":[OSD([sQuery(id+"F3.wireOp",EDGE,"E27")])],"isStart":false}),makeQuery(id+"F4.opExtrude","SWEPT_FACE",FACE,{"disambiguationData":[OSD([sQuery(id+"F3.wireOp",EDGE,"E26")])]})],"blendedInto":[makeQuery(id+"F4.opExtrude","SWEPT_FACE",FACE,{"disambiguationData":[OSD([sQuery(id+"F3.wireOp",EDGE,"E26")])]})]});
            var Q1;
            Q1=makeQuery(id+"F4.opExtrude","SWEPT_EDGE",EDGE,{"disambiguationData":[OSD([sQuery(id+"F3.wireOp",EDGE,"E21.rect.right"),sQuery(id+"F3.wireOp",EDGE,"E26")])]});
            var Q2;
            Q2=makeQuery(id+"F4.opExtrude","SWEPT_EDGE",EDGE,{"disambiguationData":[OSD([sQuery(id+"F0.wireOp",EDGE,"E18"),sQuery(id+"F3.wireOp",EDGE,"E21.rect.right")])]});
            var Q3;
            Q3=makeQuery(id+"F4.opExtrude","SWEPT_EDGE",EDGE,{"disambiguationData":[OSD([sQuery(id+"F0.wireOp",EDGE,"E18"),sQuery(id+"F3.wireOp",EDGE,"E21.rect.top")])]});
            var Q4;
            {var subQ0=sQuery(id+"F0.wireOp",EDGE,"E18");Q4=makeQuery(id+"F10.opChamfer","BLEND_EDGE",EDGE,{"blendedFrom":[makeQuery(id+"F4.opExtrude","CAP_EDGE",EDGE,{"disambiguationData":[OSD([sQuery(id+"F3.wireOp",EDGE,"E27")])],"isStart":false}),makeQuery(id+"F4.boolean.opBoolean","MERGE",FACE,{"derivedFrom":[makeQuery(id+"F1.opExtrude","SWEPT_FACE",FACE,{"disambiguationData":[OSD([subQ0])]}),makeQuery(id+"F4.opExtrude","SWEPT_FACE",FACE,{"disambiguationData":[OSD([subQ0])]})]})],"blendedInto":[makeQuery(id+"F4.boolean.opBoolean","MERGE",FACE,{"derivedFrom":[makeQuery(id+"F1.opExtrude","SWEPT_FACE",FACE,{"disambiguationData":[OSD([subQ0])]}),makeQuery(id+"F4.opExtrude","SWEPT_FACE",FACE,{"disambiguationData":[OSD([subQ0])]})]})]});}
            var Q5;
            Q5=makeQuery(id+"F4.opExtrude","CAP_EDGE",EDGE,{"disambiguationData":[OSD([sQuery(id+"F0.wireOp",EDGE,"E18")])],"isStart":false});
            var Q6;
            {var subQ0=sQuery(id+"F0.wireOp",EDGE,"E18");Q6=makeQuery(id+"F10.opChamfer","BLEND_EDGE",EDGE,{"blendedFrom":[makeQuery(id+"F4.opExtrude","CAP_EDGE",EDGE,{"disambiguationData":[OSD([sQuery(id+"F3.wireOp",EDGE,"E25.top")])],"isStart":false}),makeQuery(id+"F4.boolean.opBoolean","MERGE",FACE,{"derivedFrom":[makeQuery(id+"F1.opExtrude","SWEPT_FACE",FACE,{"disambiguationData":[OSD([subQ0])]}),makeQuery(id+"F4.opExtrude","SWEPT_FACE",FACE,{"disambiguationData":[OSD([subQ0])]})]})],"blendedInto":[makeQuery(id+"F4.boolean.opBoolean","MERGE",FACE,{"derivedFrom":[makeQuery(id+"F1.opExtrude","SWEPT_FACE",FACE,{"disambiguationData":[OSD([subQ0])]}),makeQuery(id+"F4.opExtrude","SWEPT_FACE",FACE,{"disambiguationData":[OSD([subQ0])]})]})]});}
            var Q7;
            Q7=makeQuery(id+"F4.opExtrude","SWEPT_EDGE",EDGE,{"disambiguationData":[OSD([sQuery(id+"F3.wireOp",EDGE,"E21.rect.top"),sQuery(id+"F3.wireOp",EDGE,"E25.bottom"),sQuery(id+"F3.wireOp",EDGE,"E25.left")])]});
            var Q8;
            {var subQ0=sQuery(id+"F3.wireOp",EDGE,"E21.rect.top");Q8=makeQuery(id+"F10.opChamfer","BLEND_EDGE",EDGE,{"blendedFrom":[makeQuery(id+"F4.opExtrude","CAP_EDGE",EDGE,{"disambiguationData":[OSD([sQuery(id+"F3.wireOp",EDGE,"E25.top")])],"isStart":false}),makeQuery(id+"F4.opExtrude","SWEPT_FACE",FACE,{"disambiguationData":[OSD([subQ0]),TDD([makeQuery(id+"F3.imprint","IMPRINT",EDGE,{"disambiguationData":[TD([[makeQuery(id+"F3.imprint","INTERSECT",VERTEX,{"derivedFrom":[makeQuery(id+"F1.opExtrude","CAP_EDGE",EDGE,{"disambiguationData":[OSD([sQuery(id+"F0.wireOp",EDGE,"E18")])],"isStart":true}),subQ0]}),1.0]])],"derivedFrom":subQ0})])]})],"blendedInto":[makeQuery(id+"F4.opExtrude","SWEPT_FACE",FACE,{"disambiguationData":[OSD([subQ0]),TDD([makeQuery(id+"F3.imprint","IMPRINT",EDGE,{"disambiguationData":[TD([[makeQuery(id+"F3.imprint","INTERSECT",VERTEX,{"derivedFrom":[makeQuery(id+"F1.opExtrude","CAP_EDGE",EDGE,{"disambiguationData":[OSD([sQuery(id+"F0.wireOp",EDGE,"E18")])],"isStart":true}),subQ0]}),1.0]])],"derivedFrom":subQ0})])]})]});}
            var Q9;
            Q9=makeQuery(id+"F4.opExtrude","SWEPT_EDGE",EDGE,{"disambiguationData":[OSD([sQuery(id+"F0.wireOp",EDGE,"E19"),sQuery(id+"F3.wireOp",EDGE,"E21.rect.top")])]});
            var Q10;
            Q10=makeQuery(id+"F4.opExtrude","SWEPT_EDGE",EDGE,{"disambiguationData":[OSD([sQuery(id+"F3.wireOp",EDGE,"E21.rect.top"),sQuery(id+"F3.wireOp",EDGE,"E25.bottom"),sQuery(id+"F3.wireOp",EDGE,"E25.right")])]});
            var Q11;
            Q11=makeQuery(id+"F4.opExtrude","CAP_EDGE",EDGE,{"disambiguationData":[OSD([sQuery(id+"F0.wireOp",EDGE,"E19")])],"isStart":false});
            var Q12;
            {var subQ0=sQuery(id+"F0.wireOp",EDGE,"E19");var subQ1=sQuery(id+"F0.wireOp",EDGE,"E2.rect.bottom");var subQ2=makeQuery(id+"F0.imprint","INTERSECT",VERTEX,{"disambiguationData":[OD(0.0)],"derivedFrom":[sQuery(id+"F0.wireOp",EDGE,"E14"),subQ0]});Q12=makeQuery(id+"F10.opChamfer","BLEND_EDGE",EDGE,{"blendedFrom":[makeQuery(id+"F4.opExtrude","CAP_EDGE",EDGE,{"disambiguationData":[OSD([sQuery(id+"F3.wireOp",EDGE,"E25.top")])],"isStart":false}),makeQuery(id+"F4.boolean.opBoolean","MERGE",FACE,{"derivedFrom":[makeQuery(id+"F1.opExtrude","SWEPT_FACE",FACE,{"disambiguationData":[OSD([subQ0]),TDD([makeQuery(id+"F0.imprint","IMPRINT",EDGE,{"disambiguationData":[TD([[subQ2,-1.0]])],"derivedFrom":subQ0}),makeQuery(id+"F0.imprint","IMPRINT",EDGE,{"disambiguationData":[TD([[makeQuery(id+"F0.imprint","INTERSECT",VERTEX,{"disambiguationData":[OD(1.0)],"derivedFrom":[subQ1,subQ0]}),1.0]])],"derivedFrom":subQ0}),makeQuery(id+"F0.imprint","IMPRINT",EDGE,{"disambiguationData":[TD([[makeQuery(id+"F0.imprint","INTERSECT",VERTEX,{"disambiguationData":[OD(0.0)],"derivedFrom":[subQ1,subQ0]}),-1.0]])],"derivedFrom":subQ0})])]}),makeQuery(id+"F4.opExtrude","SWEPT_FACE",FACE,{"disambiguationData":[OSD([subQ0])]})]})],"blendedInto":[makeQuery(id+"F4.boolean.opBoolean","MERGE",FACE,{"derivedFrom":[makeQuery(id+"F1.opExtrude","SWEPT_FACE",FACE,{"disambiguationData":[OSD([subQ0]),TDD([makeQuery(id+"F0.imprint","IMPRINT",EDGE,{"disambiguationData":[TD([[subQ2,-1.0]])],"derivedFrom":subQ0}),makeQuery(id+"F0.imprint","IMPRINT",EDGE,{"disambiguationData":[TD([[makeQuery(id+"F0.imprint","INTERSECT",VERTEX,{"disambiguationData":[OD(1.0)],"derivedFrom":[subQ1,subQ0]}),1.0]])],"derivedFrom":subQ0}),makeQuery(id+"F0.imprint","IMPRINT",EDGE,{"disambiguationData":[TD([[makeQuery(id+"F0.imprint","INTERSECT",VERTEX,{"disambiguationData":[OD(0.0)],"derivedFrom":[subQ1,subQ0]}),-1.0]])],"derivedFrom":subQ0})])]}),makeQuery(id+"F4.opExtrude","SWEPT_FACE",FACE,{"disambiguationData":[OSD([subQ0])]})]})]});}
            var Q13;
            {var subQ0=sQuery(id+"F3.wireOp",EDGE,"E21.rect.top");Q13=makeQuery(id+"F10.opChamfer","BLEND_EDGE",EDGE,{"blendedFrom":[makeQuery(id+"F4.opExtrude","CAP_EDGE",EDGE,{"disambiguationData":[OSD([sQuery(id+"F3.wireOp",EDGE,"E25.top")])],"isStart":false}),makeQuery(id+"F4.opExtrude","SWEPT_FACE",FACE,{"disambiguationData":[OSD([subQ0]),TDD([makeQuery(id+"F3.imprint","IMPRINT",EDGE,{"disambiguationData":[TD([[makeQuery(id+"F3.imprint","INTERSECT",VERTEX,{"derivedFrom":[subQ0,sQuery(id+"F3.wireOp",EDGE,"E25.bottom"),sQuery(id+"F3.wireOp",EDGE,"E25.right")]}),1.0]])],"derivedFrom":subQ0})])]})],"blendedInto":[makeQuery(id+"F4.opExtrude","SWEPT_FACE",FACE,{"disambiguationData":[OSD([subQ0]),TDD([makeQuery(id+"F3.imprint","IMPRINT",EDGE,{"disambiguationData":[TD([[makeQuery(id+"F3.imprint","INTERSECT",VERTEX,{"derivedFrom":[subQ0,sQuery(id+"F3.wireOp",EDGE,"E25.bottom"),sQuery(id+"F3.wireOp",EDGE,"E25.right")]}),1.0]])],"derivedFrom":subQ0})])]})]});}
            var Q14;
            {var subQ0=sQuery(id+"F3.wireOp",EDGE,"E21.rect.top");Q14=makeQuery(id+"F4.opExtrude","CAP_EDGE",EDGE,{"disambiguationData":[OSD([subQ0]),TDD([makeQuery(id+"F3.imprint","IMPRINT",EDGE,{"disambiguationData":[TD([[makeQuery(id+"F3.imprint","INTERSECT",VERTEX,{"derivedFrom":[subQ0,sQuery(id+"F3.wireOp",EDGE,"E25.bottom"),sQuery(id+"F3.wireOp",EDGE,"E25.right")]}),1.0]])],"derivedFrom":subQ0})])],"isStart":true});}
            var Q15;
            Q15=makeQuery(id+"F4.opExtrude","CAP_EDGE",EDGE,{"disambiguationData":[OSD([sQuery(id+"F3.wireOp",EDGE,"E25.right")])],"isStart":true});
            var Q16;
            {var subQ0=sQuery(id+"F3.wireOp",EDGE,"E21.rect.top");Q16=makeQuery(id+"F4.opExtrude","CAP_EDGE",EDGE,{"disambiguationData":[OSD([subQ0]),TDD([makeQuery(id+"F3.imprint","IMPRINT",EDGE,{"disambiguationData":[TD([[makeQuery(id+"F3.imprint","INTERSECT",VERTEX,{"derivedFrom":[makeQuery(id+"F1.opExtrude","CAP_EDGE",EDGE,{"disambiguationData":[OSD([sQuery(id+"F0.wireOp",EDGE,"E18")])],"isStart":true}),subQ0]}),1.0]])],"derivedFrom":subQ0})])],"isStart":true});}
            var Q17;
            Q17=makeQuery(id+"F4.opExtrude","CAP_EDGE",EDGE,{"disambiguationData":[OSD([sQuery(id+"F3.wireOp",EDGE,"E21.rect.right")])],"isStart":true});
            var Q18;
            Q18=makeQuery(id+"F4.opExtrude","CAP_EDGE",EDGE,{"disambiguationData":[OSD([sQuery(id+"F3.wireOp",EDGE,"E26")])],"isStart":true});
            var Q19;
            Q19=makeQuery(id+"F4.opExtrude","SWEPT_EDGE",EDGE,{"disambiguationData":[OSD([sQuery(id+"F3.wireOp",EDGE,"E21.rect.bottom"),sQuery(id+"F3.wireOp",EDGE,"E28")])]});
            var Q20;
            Q20=makeQuery(id+"F4.opExtrude","SWEPT_EDGE",EDGE,{"disambiguationData":[OSD([sQuery(id+"F3.wireOp",EDGE,"E21.rect.bottom"),sQuery(id+"F3.wireOp",EDGE,"E31")])]});
            var Q21;
            Q21=makeQuery(id+"F10.opChamfer","BLEND_EDGE",EDGE,{"blendedFrom":[makeQuery(id+"F4.opExtrude","CAP_EDGE",EDGE,{"disambiguationData":[OSD([sQuery(id+"F3.wireOp",EDGE,"E27")])],"isStart":false}),makeQuery(id+"F4.opExtrude","SWEPT_FACE",FACE,{"disambiguationData":[OSD([sQuery(id+"F3.wireOp",EDGE,"E28")])]})],"blendedInto":[makeQuery(id+"F4.opExtrude","SWEPT_FACE",FACE,{"disambiguationData":[OSD([sQuery(id+"F3.wireOp",EDGE,"E28")])]})]});
            var Q22;
            Q22=makeQuery(id+"F4.opExtrude","CAP_EDGE",EDGE,{"disambiguationData":[OSD([sQuery(id+"F3.wireOp",EDGE,"E21.rect.bottom")])],"isStart":false});
            var Q23;
            Q23=makeQuery(id+"F10.opChamfer","BLEND_EDGE",EDGE,{"blendedFrom":[makeQuery(id+"F4.opExtrude","CAP_EDGE",EDGE,{"disambiguationData":[OSD([sQuery(id+"F3.wireOp",EDGE,"E30")])],"isStart":false}),makeQuery(id+"F4.opExtrude","SWEPT_FACE",FACE,{"disambiguationData":[OSD([sQuery(id+"F3.wireOp",EDGE,"E21.rect.bottom")])]})],"blendedInto":[makeQuery(id+"F4.opExtrude","SWEPT_FACE",FACE,{"disambiguationData":[OSD([sQuery(id+"F3.wireOp",EDGE,"E21.rect.bottom")])]})]});
            var Q24;
            Q24=makeQuery(id+"F10.opChamfer","BLEND_EDGE",EDGE,{"blendedFrom":[makeQuery(id+"F4.opExtrude","CAP_EDGE",EDGE,{"disambiguationData":[OSD([sQuery(id+"F3.wireOp",EDGE,"E30")])],"isStart":false}),makeQuery(id+"F4.opExtrude","SWEPT_FACE",FACE,{"disambiguationData":[OSD([sQuery(id+"F3.wireOp",EDGE,"E31")])]})],"blendedInto":[makeQuery(id+"F4.opExtrude","SWEPT_FACE",FACE,{"disambiguationData":[OSD([sQuery(id+"F3.wireOp",EDGE,"E31")])]})]});
            var Q25;
            Q25=makeQuery(id+"F4.opExtrude","CAP_EDGE",EDGE,{"disambiguationData":[OSD([sQuery(id+"F3.wireOp",EDGE,"E31")])],"isStart":true});
            var Q26;
            Q26=makeQuery(id+"F4.opExtrude","CAP_EDGE",EDGE,{"disambiguationData":[OSD([sQuery(id+"F3.wireOp",EDGE,"E21.rect.bottom")])],"isStart":true});
            var Q27;
            Q27=makeQuery(id+"F4.opExtrude","SWEPT_EDGE",EDGE,{"disambiguationData":[OSD([sQuery(id+"F3.wireOp",EDGE,"E21.rect.left"),sQuery(id+"F3.wireOp",EDGE,"E29")])]});
            var Q28;
            Q28=makeQuery(id+"F10.opChamfer","BLEND_EDGE",EDGE,{"blendedFrom":[makeQuery(id+"F4.opExtrude","CAP_EDGE",EDGE,{"disambiguationData":[OSD([sQuery(id+"F3.wireOp",EDGE,"E30")])],"isStart":false}),makeQuery(id+"F4.opExtrude","SWEPT_FACE",FACE,{"disambiguationData":[OSD([sQuery(id+"F3.wireOp",EDGE,"E21.rect.left")])]})],"blendedInto":[makeQuery(id+"F4.opExtrude","SWEPT_FACE",FACE,{"disambiguationData":[OSD([sQuery(id+"F3.wireOp",EDGE,"E21.rect.left")])]})]});
            var Q29;
            Q29=makeQuery(id+"F4.opExtrude","SWEPT_EDGE",EDGE,{"disambiguationData":[OSD([sQuery(id+"F0.wireOp",EDGE,"E2.rect.top"),sQuery(id+"F3.wireOp",EDGE,"E21.rect.left")])]});
            var Q30;
            Q30=makeQuery(id+"F4.opExtrude","CAP_EDGE",EDGE,{"disambiguationData":[OSD([sQuery(id+"F3.wireOp",EDGE,"E21.rect.left")])],"isStart":true});
            var Q31;
            {var subQ0=sQuery(id+"F0.wireOp",EDGE,"E19");var subQ1=sQuery(id+"F0.wireOp",EDGE,"E2.rect.bottom");Q31=makeQuery(id+"F4.boolean.opBoolean","MERGE",EDGE,{"derivedFrom":[makeQuery(id+"F1.opExtrude","SWEPT_EDGE",EDGE,{"disambiguationData":[OSD([subQ1,subQ0]),TDD([makeQuery(id+"F0.imprint","INTERSECT",VERTEX,{"disambiguationData":[OD(1.0)],"derivedFrom":[subQ1,subQ0]})])]}),makeQuery(id+"F4.opExtrude","SWEPT_EDGE",EDGE,{"disambiguationData":[OSD([subQ1,subQ0])]})]});}
            fillet(context, id + "F11", {"entities" : qUnion([Q0, Q1, Q2, Q3, Q4, Q5, Q6, Q7, Q8, Q9, Q10, Q11, Q12, Q13, Q14, Q15, Q16, Q17, Q18, Q19, Q20, Q21, Q22, Q23, Q24, Q25, Q26, Q27, Q28, Q29, Q30, Q31]), "radius" : 0.25 * mm, "tangentPropagation" : true, "allowEdgeOverflow" : false});
        }
    });
